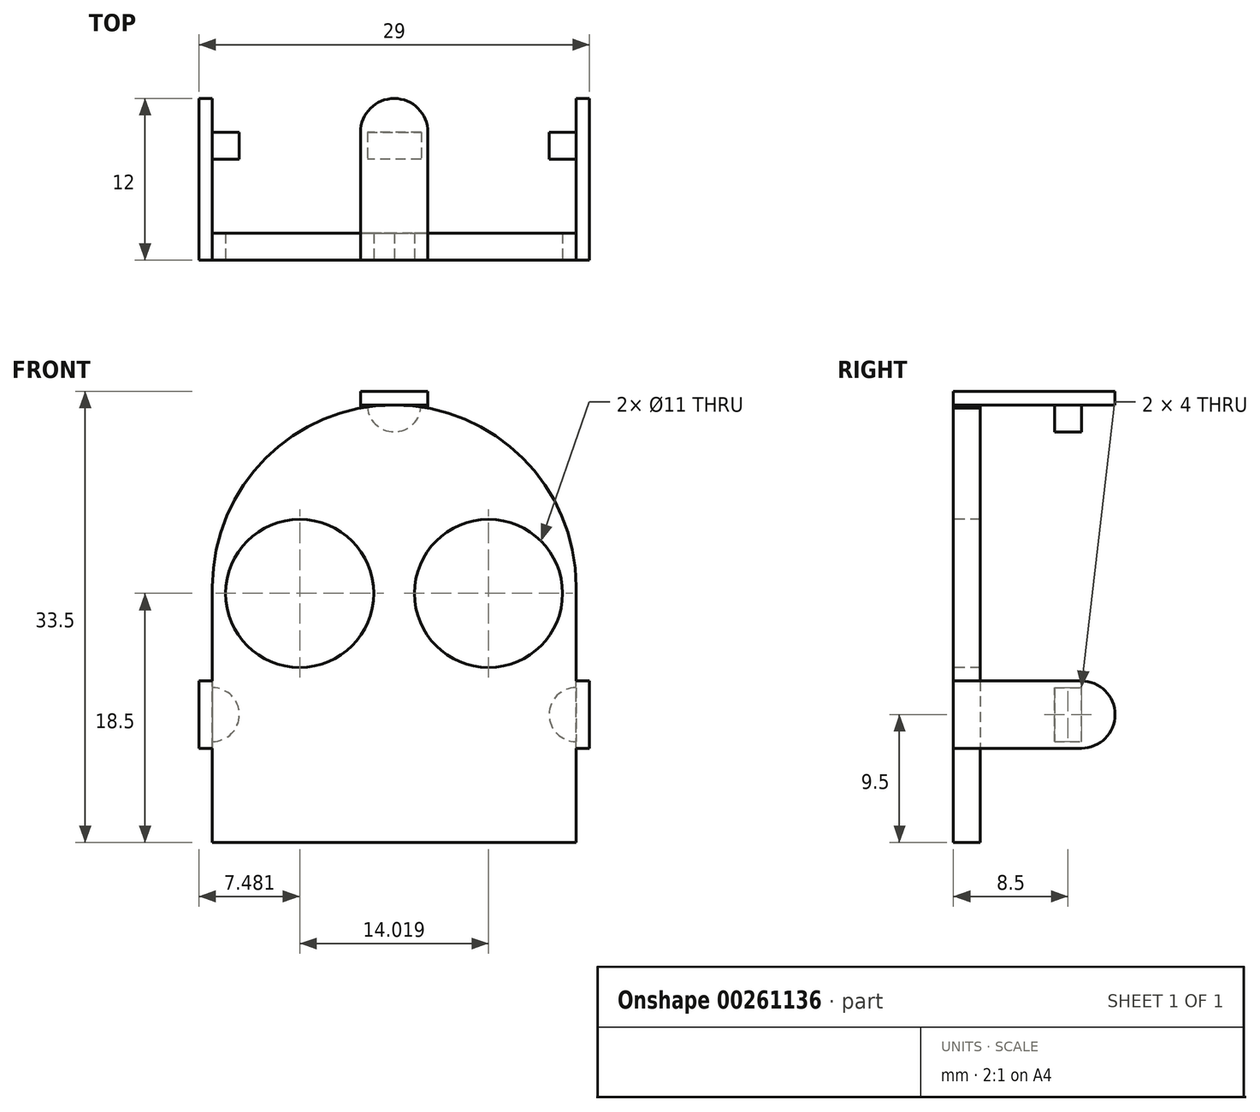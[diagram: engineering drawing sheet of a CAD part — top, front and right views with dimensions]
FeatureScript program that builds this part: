
annotation { "Feature Type Name" : "Feature", "Feature Type Description" : "" }
export const myFeature = defineFeature(function(context is Context, id is Id, definition is map)
    precondition{}
    {
        {
            var Q0;
            Q0=qCreatedBy(makeId("Front.planeOp"),FACE);
            var sketch = newSketch(context, id + "F0", { "sketchPlane" : qUnion([Q0])});
            skCircle(sketch, "E0", {"center": v(0, 0) * mm, "radius": 13.5 * mm});
            skLineSegment(sketch, "E1", {"start": v(-13.5, 0) * mm, "end": v(-13.5, -19) * mm});
            skLineSegment(sketch, "E2", {"start": v(-13.5, -19) * mm, "end": v(13.5, -19) * mm});
            skLineSegment(sketch, "E3", {"start": v(13.5, -19) * mm, "end": v(13.5, 0) * mm});
            skSolve(sketch);
        }
        {
            var Q0;
            Q0 = qSketchRegion(id + "F0", true);
            extrude(context, id + "F1", {"entities" : qUnion([Q0]), "depth" : 2 * mm});
        }
        {
            var Q0;
            Q0=qCreatedBy(makeId("Top.planeOp"),FACE);
            cPlane(context, id + "F2", {"entities" : qUnion([Q0]), "cplaneType" : CPlaneType.OFFSET, "offset" : 13.5 * mm, "width" : 150 * mm, "height" : 150 * mm});
        }
        {
            var Q0;
            Q0=qCreatedBy(id+"F2.planeOp",FACE);
            var sketch = newSketch(context, id + "F3", { "sketchPlane" : qUnion([Q0])});
            skLineSegment(sketch, "E4", {"start": v(-2.5, -2) * mm, "end": v(2.5, -2) * mm});
            skLineSegment(sketch, "E5", {"start": v(-2.5, -2) * mm, "end": v(-2.5, 7.5) * mm});
            skLineSegment(sketch, "E6", {"start": v(0, 10) * mm, "end": v(0, 10) * mm});
            skLineSegment(sketch, "E7", {"start": v(2.5, 7.5) * mm, "end": v(2.5, -2) * mm});
            skPoint(sketch, "E8.visualSharp", {"position": v(-2.5, 10) * mm});
            skArc(sketch, "E8.filletArc", {"start": v(0, 10) * mm, "mid": v(-1.77, 9.27) * mm, "end": v(-2.5, 7.5) * mm});
            skPoint(sketch, "E9.visualSharp", {"position": v(2.5, 10) * mm});
            skArc(sketch, "E9.filletArc", {"start": v(2.5, 7.5) * mm, "mid": v(1.77, 9.27) * mm, "end": v(0, 10) * mm});
            skSolve(sketch);
        }
        {
            var Q0;
            {var subQ0=sQuery(id+"F3.wireOp",EDGE,"wryP0kVR-Col3-PWuW-PCMk-qIWbX02BHaDO.right");Q0=makeQuery(id+"F3.imprint","IMPRINT",FACE,{"disambiguationData":[TD([[makeQuery(id+"F3.imprint","IMPRINT",EDGE,{"derivedFrom":subQ0}),1.0]])]});}
            var Q1;
            {var subQ0=sQuery(id+"F3.wireOp",EDGE,"wryP0kVR-Col3-PWuW-PCMk-qIWbX02BHaDO.left");Q1=makeQuery(id+"F3.imprint","IMPRINT",FACE,{"disambiguationData":[TD([[makeQuery(id+"F3.imprint","IMPRINT",EDGE,{"derivedFrom":subQ0}),-1.0]])]});}
            var Q2;
            Q2=makeQuery(id+"F3.imprint","IMPRINT",FACE,{"disambiguationData":[TD([[makeQuery(id+"F3.imprint","IMPRINT",EDGE,{"derivedFrom":sQuery(id+"F3.wireOp",EDGE,"E4")}),1.0]])]});
            extrude(context, id + "F4", {"entities" : qUnion([Q0, Q1, Q2]), "operationType" : NewBodyOperationType.ADD, "depth" : 1 * mm});
        }
        {
            var Q0;
            Q0=makeQuery(id+"F4.opExtrude","SWEPT_FACE",FACE,{"disambiguationData":[OSD([sQuery(id+"F3.wireOp",EDGE,"E4")])]});
            var sketch = newSketch(context, id + "F5", { "sketchPlane" : qUnion([Q0])});
            skCircle(sketch, "E10", {"center": v(0, 0) * mm, "radius": 13.5 * mm});
            skLineSegment(sketch, "E11", {"start": v(-2.5, 13.5) * mm, "end": v(-2.5, 13.27) * mm});
            skLineSegment(sketch, "E12", {"start": v(-2.5, 13.5) * mm, "end": v(2.5, 13.5) * mm});
            skLineSegment(sketch, "E13", {"start": v(2.5, 13.5) * mm, "end": v(2.5, 13.27) * mm});
            skSolve(sketch);
        }
        {
            var Q0;
            {var subQ0=sQuery(id+"F5.wireOp",EDGE,"E11");Q0=makeQuery(id+"F5.imprint","IMPRINT",FACE,{"disambiguationData":[TD([[makeQuery(id+"F5.imprint","IMPRINT",EDGE,{"derivedFrom":subQ0}),1.0]])]});}
            var Q1;
            {var subQ0=sQuery(id+"F5.wireOp",EDGE,"E13");Q1=makeQuery(id+"F5.imprint","IMPRINT",FACE,{"disambiguationData":[TD([[makeQuery(id+"F5.imprint","IMPRINT",EDGE,{"derivedFrom":subQ0}),-1.0]])]});}
            extrude(context, id + "F6", {"entities" : qUnion([Q0, Q1]), "oppositeDirection" : true, "depth" : 2 * mm});
        }
        {
            var Q0;
            Q0=qCreatedBy(makeId("Right.planeOp"),FACE);
            cPlane(context, id + "F7", {"entities" : qUnion([Q0]), "cplaneType" : CPlaneType.OFFSET, "offset" : 13.5 * mm, "width" : 150 * mm, "height" : 150 * mm});
        }
        {
            var Q0;
            Q0=qCreatedBy(id+"F7.planeOp",FACE);
            var sketch = newSketch(context, id + "F8", { "sketchPlane" : qUnion([Q0])});
            skLineSegment(sketch, "E14", {"start": v(-2, -7) * mm, "end": v(7.5, -7) * mm});
            skLineSegment(sketch, "E15", {"start": v(10, -9.5) * mm, "end": v(10, -9.5) * mm});
            skLineSegment(sketch, "E16", {"start": v(7.5, -12) * mm, "end": v(-2, -12) * mm});
            skLineSegment(sketch, "E17", {"start": v(-2, -12) * mm, "end": v(-2, -7) * mm});
            skPoint(sketch, "E18.visualSharp", {"position": v(10, -7) * mm});
            skArc(sketch, "E18.filletArc", {"start": v(10, -9.5) * mm, "mid": v(9.27, -7.73) * mm, "end": v(7.5, -7) * mm});
            skPoint(sketch, "E19.visualSharp", {"position": v(10, -12) * mm});
            skArc(sketch, "E19.filletArc", {"start": v(7.5, -12) * mm, "mid": v(9.27, -11.27) * mm, "end": v(10, -9.5) * mm});
            skSolve(sketch);
        }
        {
            var Q0;
            Q0 = qSketchRegion(id + "F8", true);
            extrude(context, id + "F9", {"entities" : qUnion([Q0]), "operationType" : NewBodyOperationType.ADD, "depth" : 1 * mm});
        }
        {
            var Q0;
            Q0=qCreatedBy(makeId("Right.planeOp"),FACE);
            cPlane(context, id + "F10", {"entities" : qUnion([Q0]), "cplaneType" : CPlaneType.OFFSET, "offset" : 13.5 * mm, "oppositeDirection" : true, "width" : 150 * mm, "height" : 150 * mm});
        }
        {
            var Q0;
            Q0=qCreatedBy(id+"F10.planeOp",FACE);
            var sketch = newSketch(context, id + "F11", { "sketchPlane" : qUnion([Q0])});
            skLineSegment(sketch, "E20", {"start": v(-2, -7) * mm, "end": v(-2, -12) * mm});
            skLineSegment(sketch, "E21", {"start": v(-2, -12) * mm, "end": v(7.5, -12) * mm});
            skLineSegment(sketch, "E22", {"start": v(10, -9.5) * mm, "end": v(10, -9.5) * mm});
            skLineSegment(sketch, "E23", {"start": v(7.5, -7) * mm, "end": v(-2, -7) * mm});
            skPoint(sketch, "E24.visualSharp", {"position": v(10, -7) * mm});
            skArc(sketch, "E24.filletArc", {"start": v(10, -9.5) * mm, "mid": v(9.27, -7.73) * mm, "end": v(7.5, -7) * mm});
            skPoint(sketch, "E25.visualSharp", {"position": v(10, -12) * mm});
            skArc(sketch, "E25.filletArc", {"start": v(7.5, -12) * mm, "mid": v(9.27, -11.27) * mm, "end": v(10, -9.5) * mm});
            skSolve(sketch);
        }
        {
            var Q0;
            Q0 = qSketchRegion(id + "F11", true);
            extrude(context, id + "F12", {"entities" : qUnion([Q0]), "operationType" : NewBodyOperationType.ADD, "oppositeDirection" : true, "depth" : 1 * mm});
        }
        {
            var Q0;
            Q0=makeQuery(id+"F4.opExtrude","CAP_FACE",FACE,{"disambiguationData":[OSD([sQuery(id+"F3.wireOp",EDGE,"E4"),sQuery(id+"F3.wireOp",EDGE,"E5"),sQuery(id+"F3.wireOp",EDGE,"E7"),sQuery(id+"F3.wireOp",EDGE,"E8.filletArc"),sQuery(id+"F3.wireOp",EDGE,"E9.filletArc")])],"isStart":true});
            var sketch = newSketch(context, id + "F13", { "sketchPlane" : qUnion([Q0])});
            skLineSegment(sketch, "E26", {"start": v(0, -7.5) * mm, "end": v(-2, -7.5) * mm});
            skLineSegment(sketch, "E27", {"start": v(-2, -7.5) * mm, "end": v(-2, -5.5) * mm});
            skLineSegment(sketch, "E28", {"start": v(-2, -5.5) * mm, "end": v(0, -5.5) * mm});
            skLineSegment(sketch, "E29", {"start": v(0, -5.5) * mm, "end": v(0, -7.5) * mm});
            skSolve(sketch);
        }
        {
            var Q0;
            Q0=makeQuery(id+"F13.imprint","IMPRINT",FACE,{"disambiguationData":[TD([[makeQuery(id+"F13.imprint","IMPRINT",EDGE,{"derivedFrom":sQuery(id+"F13.wireOp",EDGE,"E26")}),-1.0]])]});
            var Q1;
            Q1=sQuery(id+"F13.wireOp",EDGE,"E29");
            revolve(context, id + "F14", {"operationType" : NewBodyOperationType.ADD, "entities" : qUnion([Q0]), "axis" : qUnion([Q1]), "revolveType" : RevolveType.ONE_DIRECTION, "oppositeDirection" : true, "angle" : 180 * degree});
        }
        {
            var Q0;
            Q0=makeQuery(id+"F9.opExtrude","CAP_FACE",FACE,{"disambiguationData":[OSD([sQuery(id+"F8.wireOp",EDGE,"E14"),sQuery(id+"F8.wireOp",EDGE,"E16"),sQuery(id+"F8.wireOp",EDGE,"E17"),sQuery(id+"F8.wireOp",EDGE,"E18.filletArc"),sQuery(id+"F8.wireOp",EDGE,"E19.filletArc")])],"isStart":true});
            var sketch = newSketch(context, id + "F15", { "sketchPlane" : qUnion([Q0])});
            skLineSegment(sketch, "E30", {"start": v(-7.5, -9.5) * mm, "end": v(-7.5, -7.5) * mm});
            skPoint(sketch, "E30.startSnap0", {"position": v(0, -9.5) * mm});
            skLineSegment(sketch, "E31", {"start": v(-7.5, -7.5) * mm, "end": v(-5.5, -7.5) * mm});
            skLineSegment(sketch, "E32", {"start": v(-5.5, -7.5) * mm, "end": v(-5.5, -9.5) * mm});
            skLineSegment(sketch, "E33", {"start": v(-5.5, -9.5) * mm, "end": v(-7.5, -9.5) * mm});
            skSolve(sketch);
        }
        {
            var Q0;
            Q0=makeQuery(id+"F15.imprint","IMPRINT",FACE,{"disambiguationData":[TD([[makeQuery(id+"F15.imprint","IMPRINT",EDGE,{"derivedFrom":sQuery(id+"F15.wireOp",EDGE,"E30")}),-1.0]])]});
            var Q1;
            Q1=sQuery(id+"F15.wireOp",EDGE,"E33");
            revolve(context, id + "F16", {"operationType" : NewBodyOperationType.ADD, "entities" : qUnion([Q0]), "axis" : qUnion([Q1]), "revolveType" : RevolveType.ONE_DIRECTION, "oppositeDirection" : true, "angle" : 180 * degree});
        }
        {
            var Q0;
            Q0=makeQuery(id+"F12.opExtrude","CAP_FACE",FACE,{"disambiguationData":[OSD([sQuery(id+"F11.wireOp",EDGE,"E20"),sQuery(id+"F11.wireOp",EDGE,"E21"),sQuery(id+"F11.wireOp",EDGE,"E23"),sQuery(id+"F11.wireOp",EDGE,"E24.filletArc"),sQuery(id+"F11.wireOp",EDGE,"E25.filletArc")])],"isStart":true});
            var sketch = newSketch(context, id + "F17", { "sketchPlane" : qUnion([Q0])});
            skLineSegment(sketch, "E34", {"start": v(5.5, -9.5) * mm, "end": v(5.5, -7.5) * mm});
            skPoint(sketch, "E34.startSnap0", {"position": v(0, -9.5) * mm});
            skLineSegment(sketch, "E35", {"start": v(5.5, -7.5) * mm, "end": v(7.5, -7.5) * mm});
            skLineSegment(sketch, "E36", {"start": v(7.5, -7.5) * mm, "end": v(7.5, -9.5) * mm});
            skLineSegment(sketch, "E37", {"start": v(7.5, -9.5) * mm, "end": v(5.5, -9.5) * mm});
            skSolve(sketch);
        }
        {
            var Q0;
            Q0=makeQuery(id+"F17.imprint","IMPRINT",FACE,{"disambiguationData":[TD([[makeQuery(id+"F17.imprint","IMPRINT",EDGE,{"derivedFrom":sQuery(id+"F17.wireOp",EDGE,"E34")}),-1.0]])]});
            var Q1;
            Q1=sQuery(id+"F17.wireOp",EDGE,"E37");
            revolve(context, id + "F18", {"operationType" : NewBodyOperationType.ADD, "entities" : qUnion([Q0]), "axis" : qUnion([Q1]), "revolveType" : RevolveType.ONE_DIRECTION, "oppositeDirection" : true, "angle" : 180 * degree});
        }
        {
            var Q0;
            Q0=makeQuery(id+"F12.boolean.opBoolean","MERGE",FACE,{"derivedFrom":[makeQuery(id+"F9.boolean.opBoolean","MERGE",FACE,{"derivedFrom":[makeQuery(id+"F1.opExtrude","CAP_FACE",FACE,{"disambiguationData":[OSD([sQuery(id+"F0.wireOp",EDGE,"E0"),sQuery(id+"F0.wireOp",EDGE,"E1"),sQuery(id+"F0.wireOp",EDGE,"E2"),sQuery(id+"F0.wireOp",EDGE,"E3")])],"isStart":false}),makeQuery(id+"F9.opExtrude","SWEPT_FACE",FACE,{"disambiguationData":[OSD([sQuery(id+"F8.wireOp",EDGE,"E17")])]})]}),makeQuery(id+"F12.opExtrude","SWEPT_FACE",FACE,{"disambiguationData":[OSD([sQuery(id+"F11.wireOp",EDGE,"E20")])]})]});
            var sketch = newSketch(context, id + "F19", { "sketchPlane" : qUnion([Q0])});
            skCircle(sketch, "E38", {"center": v(-7.02, -0.5) * mm, "radius": 5.5 * mm});
            skCircle(sketch, "E39", {"center": v(7, -0.5) * mm, "radius": 5.5 * mm});
            skSolve(sketch);
        }
        {
            var Q0;
            Q0=makeQuery(id+"F19.imprint","IMPRINT",FACE,{"disambiguationData":[TD([[makeQuery(id+"F19.imprint","IMPRINT",EDGE,{"derivedFrom":sQuery(id+"F19.wireOp",EDGE,"E38")}),1.0]])]});
            var Q1;
            Q1=makeQuery(id+"F19.imprint","IMPRINT",FACE,{"disambiguationData":[TD([[makeQuery(id+"F19.imprint","IMPRINT",EDGE,{"derivedFrom":sQuery(id+"F19.wireOp",EDGE,"E39")}),1.0]])]});
            extrude(context, id + "F20", {"entities" : qUnion([Q0, Q1]), "operationType" : NewBodyOperationType.REMOVE, "oppositeDirection" : true, "depth" : 5 * mm});
        }
    });
